# Revit family: Zumtobel EXTONA
name_source: partatom
category: Lighting Fixtures
revit_build: Autodesk Revit 2018 (Build: 20170223_1515(x64)
units: mm (PartAtom-declared; Revit-internal decimal feet)

## family parameters
Cut with Voids When Loaded = No
Host = Face
Light Source = Yes
OmniClass Number = 23.80.70.11
OmniClass Title = Luminaries for Internal Lighting
Part Type = Normal
Room Calculation Point = No
Round Connector Dimension = Use Diameter
Shared = No

## types (3) — shared parameters
Assembly Code = D5020210
Body = Zumtobel_Plastics_Grey
Color Filter = 16777215
Cover = Zumtobel_PMMA_Semitransparent_SI
Description = Moisture-proof diffuser luminaire
Dimming Lamp Color Temperature Shift = <None>
Emit Shape Visible in Rendering = No
Emit from Rectangle Length = 155 mm  [stored 0.50853 ft]
Height = 105 mm  [stored 0.344488 ft]
Lamp = LED
Manufacturer = Zumtobel Lighting
Tilt Angle = -90.00°
URL = http://www.zumtobel.com
Voltage = 230 V
Width = 155 mm  [stored 0.50853 ft]
zero-valued in all types: Default Elevation

## per-type parameters (varying)
| type | Apparent Load | Emit from Rectangle Width | Length | Model | Mounting Distance | Photometric Web File |
| EXTONA L | 44 VA | 1580 mm  [stored 5.18373 ft] | 1580 mm  [stored 5.18373 ft] | 42190046 | 1000 mm  [stored 3.28084 ft] | 42190046_(STD).IES |
| EXTONA S | 15 VA | 880 mm  [stored 2.88714 ft] | 880 mm  [stored 2.88714 ft] | 42190042 | 460 mm  [stored 1.50919 ft] | 42190042_(STD).IES |
| EXTONA M | 29 VA | 1280 mm  [stored 4.19948 ft] | 1280 mm  [stored 4.19948 ft] | 42190044 | 880 mm  [stored 2.88714 ft] | 42190044_(STD).IES |

note: [stored X ft] marks values corroborated as IEEE doubles in the binary element streams (Revit-internal decimal feet)

## geometry (parser evidence)
native form markers: Sweep x5
no freeform markers — native parametric forms only
